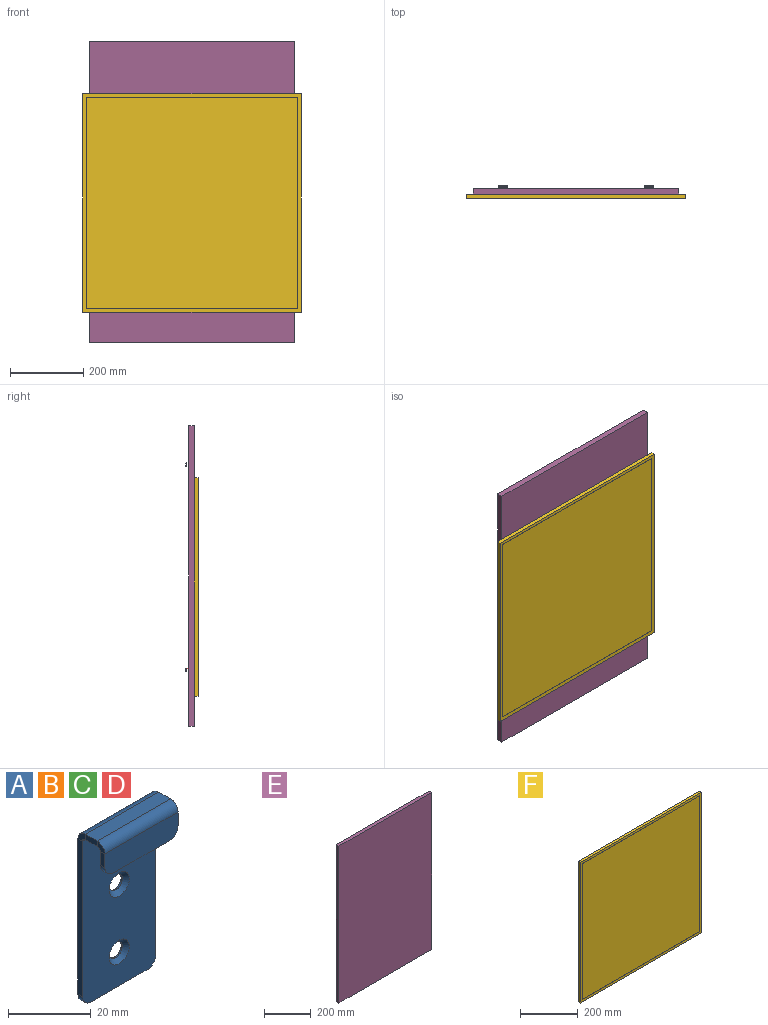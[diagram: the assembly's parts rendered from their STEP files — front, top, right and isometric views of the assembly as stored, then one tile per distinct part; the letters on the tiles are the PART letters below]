
ASSEMBLY  parts=6 mates=5
PART A: 30 faces, bbox 25x9.2x51.6 mm
  f0: plane 4x1.6mm, normal (-1,0,0), area 6.4mm2, adj f3,f4,f6,f25
  f1: plane 4x1.6mm, normal (1,0,0), area 6.4mm2, adj f3,f4,f5,f24
  f2: plane 19x1.6mm, normal (0,0,-1), area 30.4mm2, adj f3,f4,f5,f6
  f3: plane 25x7mm, normal (0,1,0), area 171.1mm2, adj f0,f1,f2,f5,f6,f27
  f4: plane 25x7mm, normal (0,-1,0), area 171.1mm2, adj f0,f1,f2,f5,f6,f26
  f5: cylinder r=3mm len=3mm, axis (0,1,0), area 7.5mm2, adj f1,f2,f3,f4
  f6: cylinder r=3mm len=3mm, axis (0,-1,0), area 7.5mm2, adj f0,f2,f3,f4
  f7: plane 4x1.6mm, normal (-1,0,0), area 6.4mm2, adj f9,f10,f21,f25
  f8: plane 4x1.6mm, normal (1,0,0), area 6.4mm2, adj f9,f10,f20,f24
  f9: plane 25x4mm, normal (0,0,-1), area 100mm2, adj f7,f8,f23,f27
  f10: plane 25x4mm, normal (0,0,1), area 100mm2, adj f7,f8,f22,f26
  f11: plane 46x1.6mm, normal (-1,0,0), area 73.6mm2, adj f16,f17,f18,f21
  f12: plane 19x1.6mm, normal (0,0,-1), area 30.4mm2, adj f16,f17,f18,f19
  f13: plane 46x1.6mm, normal (1,0,0), area 73.6mm2, adj f16,f17,f19,f20
  f14: cylinder r=2.25mm len=4.5mm, axis (0,-1,0), area 5.7mm2, adj f17,f28
  f15: cylinder r=2.25mm len=4.5mm, axis (0,-1,0), area 5.7mm2, adj f17,f29
  f16: plane 49x25mm, normal (0,-1,0), area 1146.4mm2, adj f11,f12,f13,f18,f19,f23,f28,f29
  f17: plane 49x25mm, normal (0,1,0), area 1189.3mm2, adj f11,f12,f13,f14,f15,f18,f19,f22
  f18: cylinder r=3mm len=3mm, axis (0,-1,0), area 7.5mm2, adj f11,f12,f16,f17
  f19: cylinder r=3mm len=3mm, axis (0,1,0), area 7.5mm2, adj f12,f13,f16,f17
  f20: plane 2.6x2.6mm, normal (1,0,0), area 4.5mm2, adj f8,f13,f22,f23
  f21: plane 2.6x2.6mm, normal (-1,0,0), area 4.5mm2, adj f7,f11,f22,f23
  f22: cylinder r=2.6mm len=25mm, axis (1,0,0), area 102.1mm2, adj f10,f17,f20,f21
  f23: cylinder r=1mm len=25mm, axis (1,0,0), area 39.3mm2, adj f9,f16,f20,f21
  f24: plane 2.6x2.6mm, normal (1,0,0), area 4.5mm2, adj f1,f8,f26,f27
  f25: plane 2.6x2.6mm, normal (-1,0,0), area 4.5mm2, adj f0,f7,f26,f27
  f26: cylinder r=2.6mm len=25mm, axis (1,0,0), area 102.1mm2, adj f4,f10,f24,f25
  f27: cylinder r=1mm len=25mm, axis (1,0,0), area 39.3mm2, adj f3,f9,f24,f25
  f28: cone r=3.45mm half-angle=45deg, axis (0,-1,0), area 30.4mm2, adj f14,f16
  f29: cone r=3.45mm half-angle=45deg, axis (0,-1,0), area 30.4mm2, adj f15,f16
PART B: same geometry as A
PART C: same geometry as A
PART D: same geometry as A
PART E: 42 faces, bbox 560x16x820 mm
  f0: plane 820x560mm, normal (0,1,0), area 453418.1mm2, adj f1,f2,f3,f4,f6,f7,f8,f9
  f1: plane 560x16mm, normal (0,0,1), area 8960mm2, adj f0,f2,f4,f5
  f2: plane 820x16mm, normal (-1,0,0), area 13120mm2, adj f0,f1,f3,f5
  f3: plane 560x16mm, normal (0,0,-1), area 8960mm2, adj f0,f2,f4,f5
  f4: plane 820x16mm, normal (1,0,0), area 13120mm2, adj f0,f1,f3,f5
  f5: plane 820x560mm, normal (0,-1,0), area 459200mm2, adj f1,f2,f3,f4
  f6: plane 19x1.6mm, normal (0,0,1), area 30.4mm2, adj f0,f7,f13,f14
  f7: cylinder r=3.5mm len=3.5mm, axis (0,1,0), area 8.8mm2, adj f0,f6,f8,f14
  f8: plane 49x1.6mm, normal (-1,0,0), area 78.4mm2, adj f0,f7,f9,f14
  f9: cylinder r=3.5mm len=3.5mm, axis (0,1,0), area 8.8mm2, adj f0,f8,f10,f14
  f10: plane 19x1.6mm, normal (0,0,-1), area 30.4mm2, adj f0,f9,f11,f14
  f11: cylinder r=3.5mm len=3.5mm, axis (0,1,0), area 8.8mm2, adj f0,f10,f12,f14
  f12: plane 49x1.6mm, normal (1,0,0), area 78.4mm2, adj f0,f11,f13,f14
  f13: cylinder r=3.5mm len=3.5mm, axis (0,1,0), area 8.8mm2, adj f0,f6,f12,f14
  f14: plane 56x26mm, normal (0,1,0), area 1445.5mm2, adj f6,f7,f8,f9,f10,f11,f12,f13
  f15: cylinder r=3.5mm len=3.5mm, axis (0,1,0), area 8.8mm2, adj f0,f16,f22,f23
  f16: plane 19x1.6mm, normal (0,0,-1), area 30.4mm2, adj f0,f15,f17,f23
  f17: cylinder r=3.5mm len=3.5mm, axis (0,1,0), area 8.8mm2, adj f0,f16,f18,f23
  f18: plane 49x1.6mm, normal (1,0,0), area 78.4mm2, adj f0,f17,f19,f23
  f19: cylinder r=3.5mm len=3.5mm, axis (0,1,0), area 8.8mm2, adj f0,f18,f20,f23
  f20: plane 19x1.6mm, normal (0,0,1), area 30.4mm2, adj f0,f19,f21,f23
  f21: cylinder r=3.5mm len=3.5mm, axis (0,1,0), area 8.8mm2, adj f0,f20,f22,f23
  f22: plane 49x1.6mm, normal (-1,0,0), area 78.4mm2, adj f0,f15,f21,f23
  f23: plane 56x26mm, normal (0,1,0), area 1445.5mm2, adj f15,f16,f17,f18,f19,f20,f21,f22
  f24: cylinder r=3.5mm len=3.5mm, axis (0,1,0), area 8.8mm2, adj f0,f25,f31,f32
  f25: plane 49x1.6mm, normal (-1,0,0), area 78.4mm2, adj f0,f24,f26,f32
  f26: cylinder r=3.5mm len=3.5mm, axis (0,1,0), area 8.8mm2, adj f0,f25,f27,f32
  f27: plane 19x1.6mm, normal (0,0,-1), area 30.4mm2, adj f0,f26,f28,f32
  f28: cylinder r=3.5mm len=3.5mm, axis (0,1,0), area 8.8mm2, adj f0,f27,f29,f32
  f29: plane 49x1.6mm, normal (1,0,0), area 78.4mm2, adj f0,f28,f30,f32
  f30: cylinder r=3.5mm len=3.5mm, axis (0,1,0), area 8.8mm2, adj f0,f29,f31,f32
  f31: plane 19x1.6mm, normal (0,0,1), area 30.4mm2, adj f0,f24,f30,f32
  f32: plane 56x26mm, normal (0,1,0), area 1445.5mm2, adj f24,f25,f26,f27,f28,f29,f30,f31
  f33: plane 49x1.6mm, normal (1,0,0), area 78.4mm2, adj f0,f34,f40,f41
  f34: cylinder r=3.5mm len=3.5mm, axis (0,1,0), area 8.8mm2, adj f0,f33,f35,f41
  f35: plane 19x1.6mm, normal (0,0,1), area 30.4mm2, adj f0,f34,f36,f41
  f36: cylinder r=3.5mm len=3.5mm, axis (0,1,0), area 8.8mm2, adj f0,f35,f37,f41
  f37: plane 49x1.6mm, normal (-1,0,0), area 78.4mm2, adj f0,f36,f38,f41
  f38: cylinder r=3.5mm len=3.5mm, axis (0,1,0), area 8.8mm2, adj f0,f37,f39,f41
  f39: plane 19x1.6mm, normal (0,0,-1), area 30.4mm2, adj f0,f38,f40,f41
  f40: cylinder r=3.5mm len=3.5mm, axis (0,1,0), area 8.8mm2, adj f0,f33,f39,f41
  f41: plane 56x26mm, normal (0,1,0), area 1445.5mm2, adj f33,f34,f35,f36,f37,f38,f39,f40
PART F: 11 faces, bbox 595x10.5x595 mm
  f0: plane 595x10.5mm, normal (1,0,0), area 6247.5mm2, adj f1,f3,f4,f5
  f1: plane 595x10.5mm, normal (0,0,1), area 6247.5mm2, adj f0,f2,f4,f5
  f2: plane 595x10.5mm, normal (-1,0,0), area 6247.5mm2, adj f1,f3,f4,f5
  f3: plane 595x10.5mm, normal (0,0,-1), area 6247.5mm2, adj f0,f2,f4,f5
  f4: plane 595x595mm, normal (0,1,0), area 354025mm2, adj f0,f1,f2,f3
  f5: plane 595x595mm, normal (0,-1,0), area 23400mm2, adj f0,f1,f2,f3,f6,f7,f8,f9
  f6: plane 575x1mm, normal (0,0,-1), area 575mm2, adj f5,f7,f9,f10
  f7: plane 575x1mm, normal (1,0,0), area 575mm2, adj f5,f6,f8,f10
  f8: plane 575x1mm, normal (0,0,1), area 575mm2, adj f5,f7,f9,f10
  f9: plane 575x1mm, normal (-1,0,0), area 575mm2, adj f5,f6,f8,f10
  f10: plane 575x575mm, normal (0,-1,0), area 330625mm2, adj f6,f7,f8,f9
PLACE A rot(axis=(0,0,1),180deg) t=(100,0,307.06)mm
PLACE B rot(axis=(0,0,1),180deg) t=(-300,0,307.06)mm
PLACE C rot(axis=(0,0,1),180deg) t=(100,0,-252.94)mm
PLACE D rot(axis=(0,0,1),180deg) t=(-300,0,-252.94)mm
PLACE E t=(-3345,0,-604.94)mm
PLACE F t=(0,-26.5,-29.94)mm
MATE fastened F.f4 <-> E.f5  axis (0,1,0) through (0,-16,-29.94)mm
MATE fastened D.f17 <-> E.f32  axis (0,-1,0) through (-200,-1.6,-302.94)mm
MATE fastened A.f17 <-> E.f14  axis (0,-1,0) through (200,-1.6,257.06)mm
MATE fastened C.f17 <-> E.f41  axis (0,-1,0) through (200,-1.6,-302.94)mm
MATE fastened B.f17 <-> E.f23  axis (0,-1,0) through (-200,-1.6,257.06)mm
